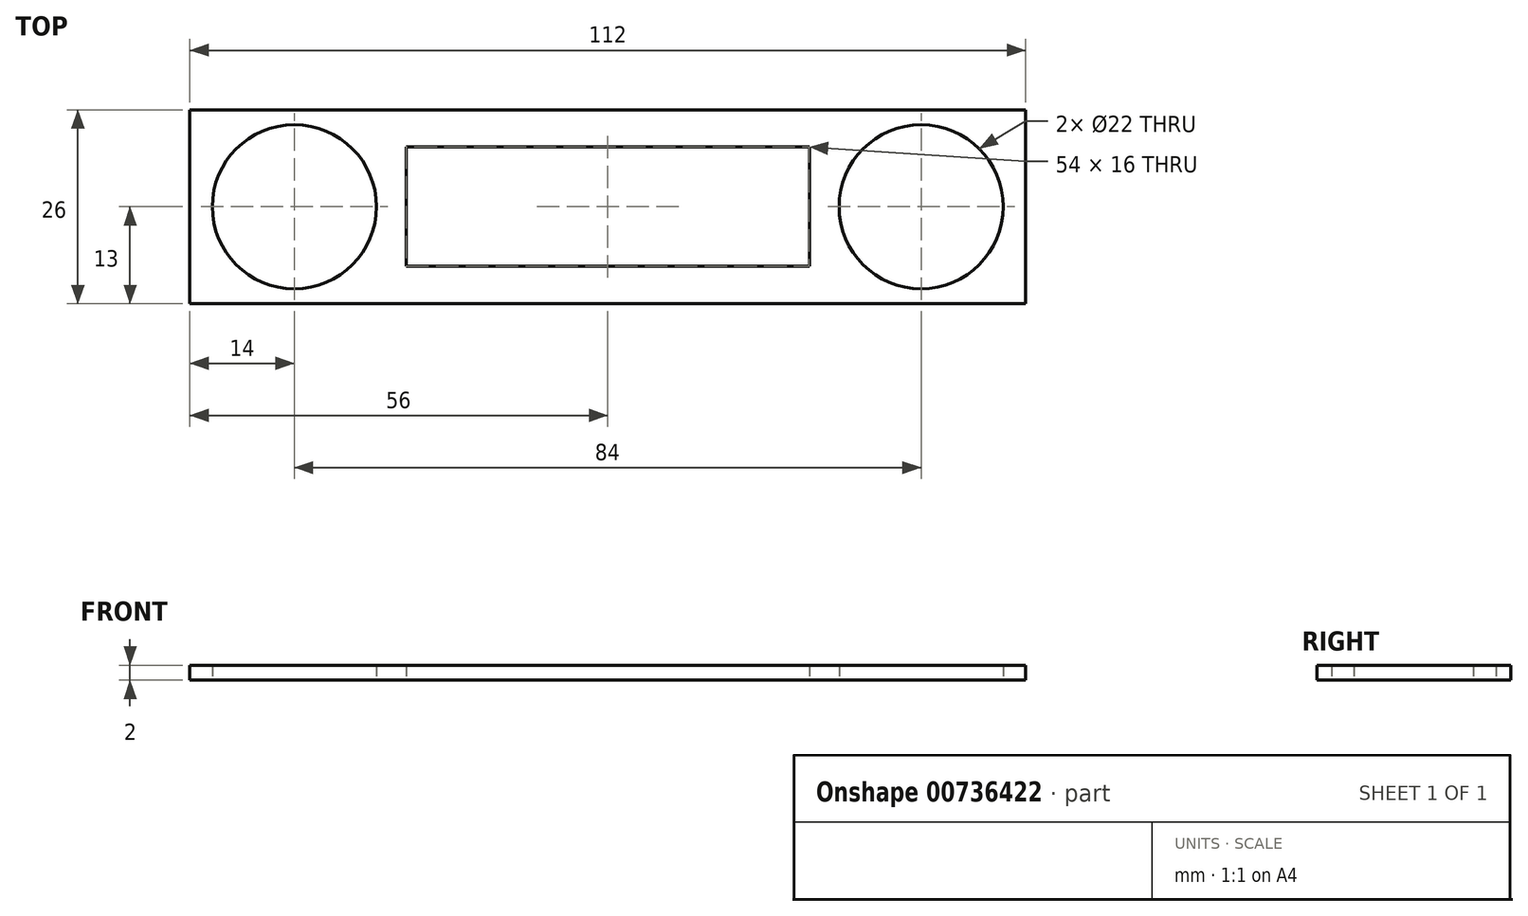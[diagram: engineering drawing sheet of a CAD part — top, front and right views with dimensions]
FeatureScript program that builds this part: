
annotation { "Feature Type Name" : "Feature", "Feature Type Description" : "" }
export const myFeature = defineFeature(function(context is Context, id is Id, definition is map)
    precondition{}
    {
        {
            var Q0;
            Q0=qCreatedBy(makeId("Top.planeOp"),FACE);
            var sketch = newSketch(context, id + "F0", { "sketchPlane" : qUnion([Q0])});
            skLineSegment(sketch, "E0.bottom", {"start": v(56, 13) * mm, "end": v(-56, 13) * mm});
            skLineSegment(sketch, "E0.top", {"start": v(56, -13) * mm, "end": v(-56, -13) * mm});
            skLineSegment(sketch, "E0.left", {"start": v(56, 13) * mm, "end": v(56, -13) * mm});
            skLineSegment(sketch, "E0.right", {"start": v(-56, 13) * mm, "end": v(-56, -13) * mm});
            skPoint(sketch, "E0.middle", {"position": v(0, 0) * mm});
            skLineSegment(sketch, "E1", {"start": v(0, 0) * mm, "end": v(42, 0) * mm, "construction": true});
            skLineSegment(sketch, "E2", {"start": v(0, 0) * mm, "end": v(-42, 0) * mm, "construction": true});
            skCircle(sketch, "E3", {"center": v(-42, 0) * mm, "radius": 11 * mm});
            skCircle(sketch, "E4", {"center": v(42, 0) * mm, "radius": 11 * mm});
            skLineSegment(sketch, "E5.bottom", {"start": v(27, 8) * mm, "end": v(-27, 8) * mm});
            skLineSegment(sketch, "E5.top", {"start": v(27, -8) * mm, "end": v(-27, -8) * mm});
            skLineSegment(sketch, "E5.left", {"start": v(27, 8) * mm, "end": v(27, -8) * mm});
            skLineSegment(sketch, "E5.right", {"start": v(-27, 8) * mm, "end": v(-27, -8) * mm});
            skSolve(sketch);
        }
        {
            var Q0;
            Q0=makeQuery(id+"F0.imprint","IMPRINT",FACE,{"disambiguationData":[TD([[makeQuery(id+"F0.imprint","IMPRINT",EDGE,{"derivedFrom":sQuery(id+"F0.wireOp",EDGE,"E0.bottom")}),1.0]])]});
            extrude(context, id + "F1", {"entities" : qUnion([Q0]), "depth" : 2 * mm, "offsetDistance" : 25 * mm});
        }
    });
